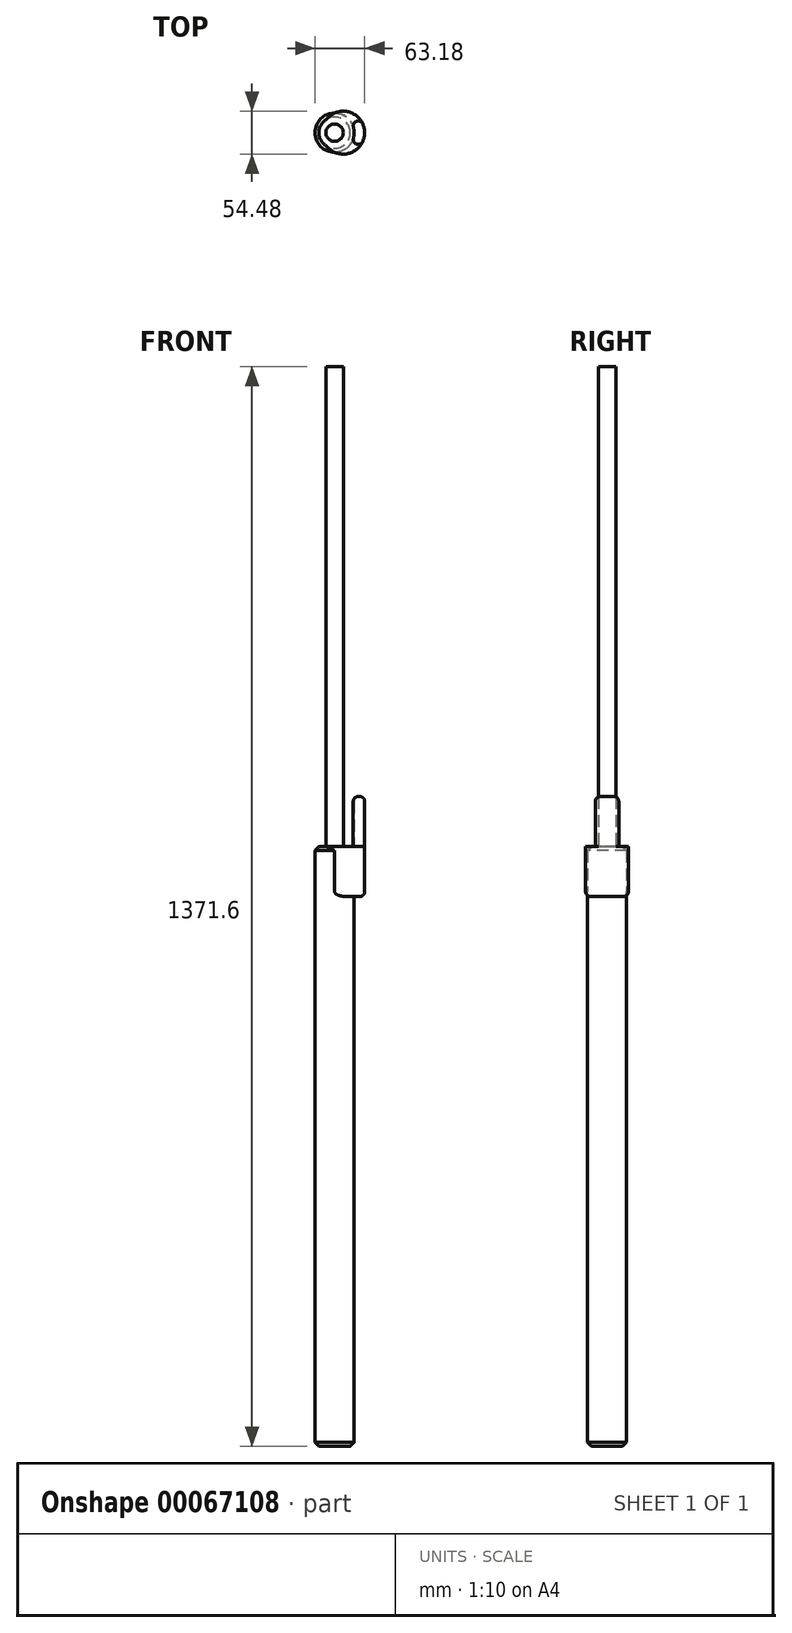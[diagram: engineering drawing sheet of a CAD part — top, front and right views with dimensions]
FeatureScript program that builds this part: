
annotation { "Feature Type Name" : "Feature", "Feature Type Description" : "" }
export const myFeature = defineFeature(function(context is Context, id is Id, definition is map)
    precondition{}
    {
        {
            var Q0;
            Q0=qCreatedBy(makeId("Top.planeOp"),FACE);
            var sketch = newSketch(context, id + "F0", { "sketchPlane" : qUnion([Q0])});
            skCircle(sketch, "E0", {"center": v(0, 0) * mm, "radius": 24.92 * mm});
            skArc(sketch, "E1", {"start": v(0, -24.92) * mm, "mid": v(38.26, 0) * mm, "end": v(0, 24.92) * mm});
            skSolve(sketch);
        }
        {
            var Q0;
            {var subQ0=sQuery(id+"F0.wireOp",EDGE,"E1");var subQ1=sQuery(id+"F0.wireOp",EDGE,"E0");var subQ2=makeQuery(id+"F0.imprint","INTERSECT",VERTEX,{"disambiguationData":[OD(0.0)],"derivedFrom":[subQ1,subQ0]});Q0=makeQuery(id+"F0.imprint","IMPRINT",FACE,{"disambiguationData":[TD([[makeQuery(id+"F0.imprint","IMPRINT",EDGE,{"disambiguationData":[TD([[subQ2,1.0]])],"derivedFrom":subQ1}),1.0]])]});}
            extrude(context, id + "F1", {"entities" : qUnion([Q0]), "oppositeDirection" : true, "depth" : 762 * mm});
        }
        {
            var Q0;
            {var subQ0=sQuery(id+"F0.wireOp",EDGE,"E1");Q0=makeQuery(id+"F0.imprint","IMPRINT",FACE,{"disambiguationData":[TD([[makeQuery(id+"F0.imprint","IMPRINT",EDGE,{"derivedFrom":subQ0}),1.0]])]});}
            extrude(context, id + "F2", {"entities" : qUnion([Q0]), "operationType" : NewBodyOperationType.ADD, "depth" : 63.5 * mm, "hasSecondDirection" : true, "secondDirectionOppositeDirection" : true, "secondDirectionDepth" : 63.5 * mm});
        }
        {
            var Q0;
            Q0=qCreatedBy(makeId("Top.planeOp"),FACE);
            var sketch = newSketch(context, id + "F3", { "sketchPlane" : qUnion([Q0])});
            skCircle(sketch, "E2", {"center": v(0, 0) * mm, "radius": 11.07 * mm});
            skSolve(sketch);
        }
        {
            var Q0;
            Q0=makeQuery(id+"F3.imprint","IMPRINT",FACE,{"disambiguationData":[TD([[makeQuery(id+"F3.imprint","IMPRINT",EDGE,{"derivedFrom":sQuery(id+"F3.wireOp",EDGE,"E2")}),1.0]])]});
            extrude(context, id + "F4", {"entities" : qUnion([Q0]), "operationType" : NewBodyOperationType.ADD, "depth" : 609.6 * mm});
        }
        {
            var Q0;
            Q0=makeQuery(id+"F2.opExtrude","CAP_EDGE",EDGE,{"disambiguationData":[OSD([sQuery(id+"F0.wireOp",EDGE,"E0")])],"isStart":false});
            var Q1;
            Q1=makeQuery(id+"F2.opExtrude","CAP_EDGE",EDGE,{"disambiguationData":[OSD([sQuery(id+"F0.wireOp",EDGE,"E1")])],"isStart":false});
            var Q2;
            {var subQ0=sQuery(id+"F0.wireOp",EDGE,"E1");var subQ1=sQuery(id+"F0.wireOp",EDGE,"E0");Q2=makeQuery(id+"F2.boolean.opBoolean","SPLIT",EDGE,{"disambiguationData":[TD([makeQuery(id+"F2.opExtrude","CAP_FACE",FACE,{"disambiguationData":[OSD([subQ1,subQ0])],"isStart":true})])],"derivedFrom":makeQuery(id+"F2.opExtrude","SWEPT_EDGE",EDGE,{"disambiguationData":[OSD([subQ1,subQ0]),TDD([makeQuery(id+"F0.imprint","INTERSECT",VERTEX,{"disambiguationData":[OD(0.0)],"derivedFrom":[subQ1,subQ0]})])]})});}
            var Q3;
            Q3=makeQuery(id+"F2.opExtrude","CAP_EDGE",EDGE,{"disambiguationData":[OSD([sQuery(id+"F0.wireOp",EDGE,"E0")])],"isStart":true});
            var Q4;
            {var subQ0=sQuery(id+"F0.wireOp",EDGE,"E1");var subQ1=sQuery(id+"F0.wireOp",EDGE,"E0");Q4=makeQuery(id+"F2.boolean.opBoolean","SPLIT",EDGE,{"disambiguationData":[TD([makeQuery(id+"F2.opExtrude","CAP_FACE",FACE,{"disambiguationData":[OSD([subQ1,subQ0])],"isStart":true})])],"derivedFrom":makeQuery(id+"F2.opExtrude","SWEPT_EDGE",EDGE,{"disambiguationData":[OSD([subQ1,subQ0]),TDD([makeQuery(id+"F0.imprint","INTERSECT",VERTEX,{"disambiguationData":[OD(1.0)],"derivedFrom":[subQ1,subQ0]})])]})});}
            var Q5;
            Q5=makeQuery(id+"F2.opExtrude","CAP_EDGE",EDGE,{"disambiguationData":[OSD([sQuery(id+"F0.wireOp",EDGE,"E1")])],"isStart":true});
            fillet(context, id + "F5", {"entities" : qUnion([Q0, Q1, Q2, Q3, Q4, Q5]), "radius" : 6.35 * mm, "tangentPropagation" : true, "allowEdgeOverflow" : false});
        }
        {
            var Q0;
            Q0=makeQuery(id+"F2.boolean.opBoolean","SPLIT",EDGE,{"disambiguationData":[OD(0.0)],"derivedFrom":makeQuery(id+"F1.opExtrude","CAP_EDGE",EDGE,{"disambiguationData":[OSD([sQuery(id+"F0.wireOp",EDGE,"E0")])],"isStart":true})});
            var Q1;
            Q1=makeQuery(id+"F1.opExtrude","CAP_EDGE",EDGE,{"disambiguationData":[OSD([sQuery(id+"F0.wireOp",EDGE,"E0")])],"isStart":false});
            chamfer(context, id + "F6", {"entities" : qUnion([Q0, Q1]), "width" : 5.08 * mm, "tangentPropagation" : true});
        }
    });
